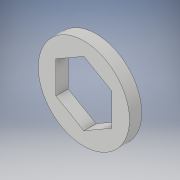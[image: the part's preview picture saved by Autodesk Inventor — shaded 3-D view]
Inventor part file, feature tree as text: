
AUTODESK INVENTOR PART (.ipt)
format: ipt  version: 2017 (Build 210142000, 142)  size: 100,864 bytes
history: native  units: in
note: dims shown in document units (in); Inventor stores cm internally (conversion verified against a paired STEP export)
features: extrude x1, sketch x1
ambient origin geometry x8: Origin, YZ Plane, XZ Plane, XY Plane, X Axis, Y Axis, Z Axis, Center Point
bodies: Solid1 (feature_tree)
feature tree (2):
  extrude  "Extrusion1"  Depth=0.11in TaperAngle=0.0deg
  sketch  "Sketch1"  dims[d0=0.819in d1=0.11in d2=0.0in]
